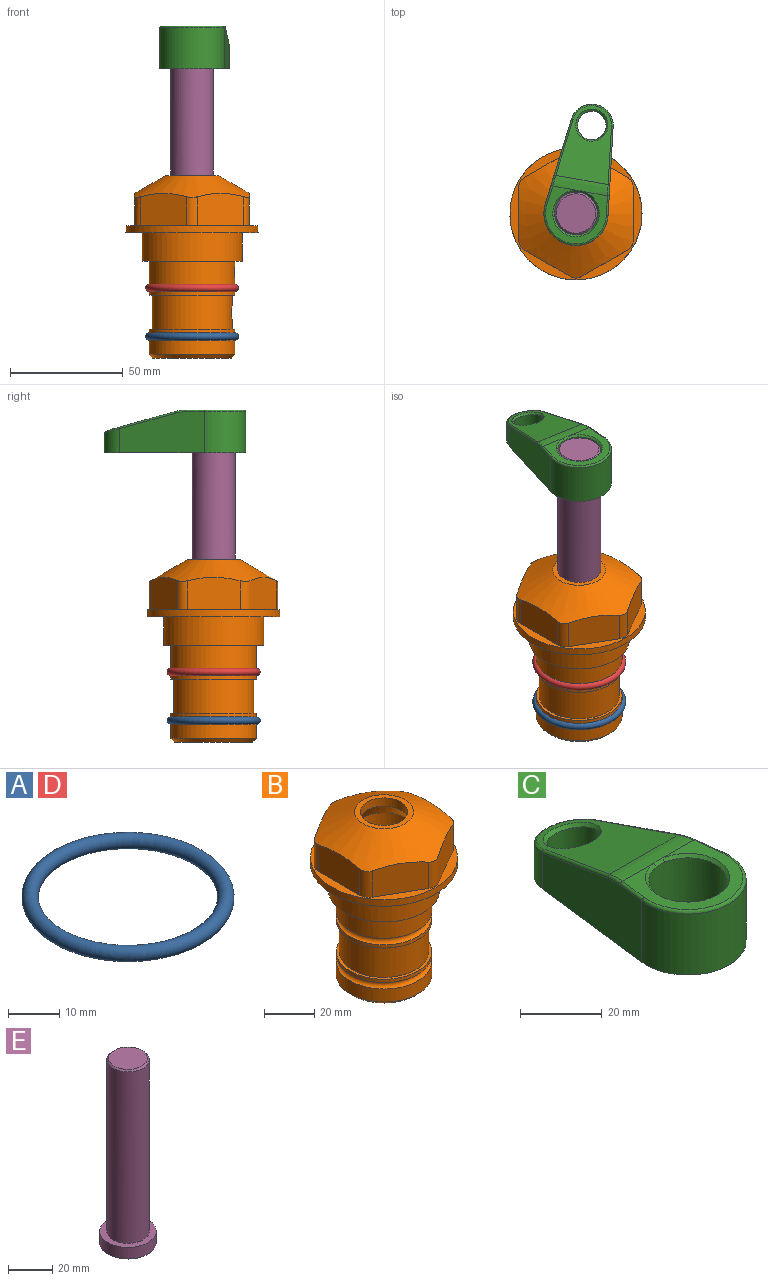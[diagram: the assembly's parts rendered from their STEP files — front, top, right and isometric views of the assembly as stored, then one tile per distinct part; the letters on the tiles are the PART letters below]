
ASSEMBLY  parts=5 mates=4
PART A: 1 faces, bbox 44.7x44.7x3.2 mm
  f0: torus R=19.05mm, axis (0,0,1), area 1193.9mm2
PART B: 36 faces, bbox 58.7x58.7x81 mm
  f0: cylinder r=17.78mm len=35.56mm, axis (0,0,1), area 1670.8mm2, adj f23,f24,f31
  f1: cylinder r=19.05mm len=38.1mm, axis (0,0,1), area 1191.9mm2, adj f26,f27,f30
  f2: plane 58.66x58.66mm, normal (0,0,-1), area 1150.6mm2, adj f3,f28
  f3: cylinder r=29.33mm len=58.66mm, axis (0,0,-1), area 585.1mm2, adj f2,f4
  f4: plane 58.66x58.66mm, normal (0,0,1), area 475.9mm2, adj f3,f5,f6,f7,f8,f9,f10,f11
  f5: plane 20.32x14.34mm, normal (-0.5,0.87,0), area 324.4mm2, adj f4,f15,f16,f17
  f6: plane 20.32x14.34mm, normal (0.5,0.87,0), area 324.4mm2, adj f4,f14,f15,f17
  f7: plane 23.48x14.34mm, normal (1,0,0), area 324.4mm2, adj f4,f13,f14,f17
  f8: plane 20.32x14.34mm, normal (0.5,-0.87,0), area 324.4mm2, adj f4,f12,f13,f17
  f9: plane 20.32x14.34mm, normal (-0.5,-0.87,0), area 324.4mm2, adj f4,f11,f12,f17
  f10: plane 23.48x14.34mm, normal (-1,0,0), area 324.4mm2, adj f4,f11,f16,f17
  f11: cylinder r=5.08mm len=12.85mm, axis (0,0,-1), area 67.2mm2, adj f4,f9,f10,f17
  f12: cylinder r=5.08mm len=12.85mm, axis (0,0,-1), area 67.2mm2, adj f4,f8,f9,f17
  f13: cylinder r=5.08mm len=12.85mm, axis (0,0,-1), area 67.2mm2, adj f4,f7,f8,f17
  f14: cylinder r=5.08mm len=12.85mm, axis (0,0,-1), area 67.2mm2, adj f4,f6,f7,f17
  f15: cylinder r=5.08mm len=12.85mm, axis (0,0,-1), area 67.2mm2, adj f4,f5,f6,f17
  f16: cylinder r=5.08mm len=12.85mm, axis (0,0,-1), area 67.2mm2, adj f4,f5,f10,f17
  f17: cone r=11.73mm half-angle=60deg, axis (0,0,-1), area 2071.8mm2, adj f5,f6,f7,f8,f9,f10,f11,f12
  f18: plane 23.46x23.46mm, normal (0,0,1), area 147.4mm2, adj f17,f35
  f19: plane 34.93x34.93mm, normal (0,0,-1), area 958mm2, adj f29
  f20: cylinder r=19.05mm len=38.1mm, axis (0,0,1), area 760.1mm2, adj f21,f29
  f21: torus R=19.05mm, axis (0,0,1), area 565.3mm2, adj f20,f22
  f22: cylinder r=19.05mm len=38.1mm, axis (0,0,1), area 190mm2, adj f21,f23
  f23: plane 38.1x38.1mm, normal (0,0,1), area 146.9mm2, adj f0,f22
  f24: plane 38.1x38.1mm, normal (0,0,-1), area 146.9mm2, adj f0,f25
  f25: cylinder r=19.05mm len=38.1mm, axis (0,0,1), area 190mm2, adj f24,f26
  f26: torus R=19.05mm, axis (0,0,1), area 565.3mm2, adj f1,f25
  f27: plane 44.45x44.45mm, normal (0,0,-1), area 411.7mm2, adj f1,f28
  f28: cylinder r=22.23mm len=44.45mm, axis (0,0,1), area 1773.5mm2, adj f2,f27
  f29: cone r=19.05mm half-angle=45deg, axis (0,0,1), area 257.5mm2, adj f19,f20
  f30: cylinder r=3.17mm len=6.75mm, axis (-1,0,0), area 128mm2, adj f1,f33
  f31: cylinder r=3.17mm len=6.35mm, axis (-1,0,0), area 102.5mm2, adj f0,f33
  f32: plane 25.4x25.4mm, normal (0,0,1), area 506.7mm2, adj f33
  f33: cylinder r=12.7mm len=66.42mm, axis (0,0,-1), area 5236.2mm2, adj f30,f31,f32,f34
  f34: cone r=9.53mm half-angle=30deg, axis (0,0,-1), area 443.4mm2, adj f33,f35
  f35: cylinder r=9.53mm len=19.05mm, axis (0,0,-1), area 240.9mm2, adj f18,f34
PART C: 31 faces, bbox 31.7x65.5x19.8 mm
  f0: plane 39.12x18.26mm, normal (0.99,0.12,0), area 612.2mm2, adj f1,f4,f7,f11,f13,f15
  f1: cylinder r=9.53mm len=18.91mm, axis (0,0,-1), area 296.1mm2, adj f0,f2,f7,f17
  f2: plane 39.12x18.26mm, normal (-0.99,0.12,0), area 612.2mm2, adj f1,f4,f7,f12,f14,f16
  f3: cylinder r=6.35mm len=12.7mm, axis (0,0,-1), area 362.4mm2, adj f7,f18
  f4: cylinder r=14.29mm len=28.58mm, axis (0,0,-1), area 882.2mm2, adj f0,f2,f7,f10
  f5: cylinder r=9.53mm len=19.05mm, axis (0,0,-1), area 1092.6mm2, adj f7,f19,f20
  f6: plane 26.99x23.69mm, normal (0,0,1), area 216.2mm2, adj f9,f10,f11,f12,f19
  f7: plane 63.5x28.58mm, normal (0,0,-1), area 661.8mm2, adj f0,f1,f2,f3,f4,f5,f22,f23
  f8: plane 33.52x23.6mm, normal (0,0.26,0.97), area 486mm2, adj f9,f15,f16,f17,f18
  f9: cylinder r=19.05mm len=24.72mm, axis (1,0,0), area 120.4mm2, adj f6,f8,f13,f14,f20
  f10: torus R=13.49mm, axis (0,0,1), area 59mm2, adj f4,f6,f11,f12
  f11: cylinder r=0.79mm len=8.67mm, axis (0.12,-0.99,0), area 10.8mm2, adj f0,f6,f10,f13
  f12: cylinder r=0.79mm len=8.67mm, axis (0.12,0.99,0), area 10.8mm2, adj f2,f6,f10,f14
  f13: bspline ~4.95x1.42mm, area 6.1mm2, adj f0,f9,f11,f15
  f14: bspline ~4.95x1.42mm, area 6.1mm2, adj f2,f9,f12,f16
  f15: cylinder r=0.79mm len=25.95mm, axis (0.12,-0.96,0.26), area 32.9mm2, adj f0,f8,f13,f17
  f16: cylinder r=0.79mm len=25.95mm, axis (0.12,0.96,-0.26), area 32.9mm2, adj f2,f8,f14,f17
  f17: bspline ~18.91x8.38mm, area 30mm2, adj f1,f8,f15,f16
  f18: bspline ~14.29x14.29mm, area 48.3mm2, adj f3,f8
  f19: cone r=9.53mm half-angle=45deg, axis (0,0,1), area 66.5mm2, adj f5,f6,f20
  f20: bspline ~3.22x0.96mm, area 3.5mm2, adj f5,f9,f19
  f21: plane 2.75x2.72mm, normal (0,0,-1), area 2.9mm2, adj f23,f25,f28
  f22: plane 23.05x15.88mm, normal (-0.99,-0.12,0), area 323.6mm2, adj f7,f25,f26,f27,f28,f29
  f23: plane 23.05x15.88mm, normal (0.99,-0.12,0), area 323.6mm2, adj f7,f21,f25,f27,f28,f30
  f24: cylinder r=9.53mm len=10.69mm, axis (0,0,-1), area 114.7mm2, adj f7,f27,f29,f30
  f25: cylinder r=12.7mm len=20.59mm, axis (0,0,-1), area 381.1mm2, adj f7,f21,f22,f23,f26,f28
  f26: plane 2.75x2.72mm, normal (0,0,-1), area 2.9mm2, adj f22,f25,f28
  f27: plane 19.72x18.37mm, normal (0,-0.26,-0.97), area 291.8mm2, adj f22,f23,f24,f28,f29,f30
  f28: cylinder r=15.88mm len=19.92mm, axis (1,0,0), area 54.8mm2, adj f21,f22,f23,f25,f26,f27
  f29: cylinder r=1.59mm len=11mm, axis (0,0,-1), area 34.7mm2, adj f7,f22,f24,f27
  f30: cylinder r=1.59mm len=11mm, axis (0,0,-1), area 34.7mm2, adj f7,f23,f24,f27
PART D: same geometry as A
PART E: 6 faces, bbox 25.4x25.4x101.6 mm
  f0: plane 17.46x17.46mm, normal (0,0,1), area 239.5mm2, adj f5
  f1: plane 25.4x25.4mm, normal (0,0,-1), area 506.7mm2, adj f2
  f2: cylinder r=12.7mm len=25.4mm, axis (0,0,1), area 506.7mm2, adj f1,f3
  f3: plane 25.4x25.4mm, normal (0,0,1), area 221.7mm2, adj f2,f4
  f4: cylinder r=9.53mm len=94.46mm, axis (0,0,1), area 5653mm2, adj f3,f5
  f5: cone r=8.73mm half-angle=45deg, axis (0,0,-1), area 64.4mm2, adj f0,f4
PLACE A t=(0,0,-21.59)mm
PLACE B at identity fixed
PLACE C rot(axis=(0,0,-1),10.2deg) t=(0,0,28.35)mm
PLACE D at identity
PLACE E rot(axis=(0,0,-1),10.2deg) t=(0,0,27.55)mm
MATE cylindrical E.f2 <-> B.f0  axis (0,0,-1) through (0,0,-10.55)mm
MATE fastened D.f0 <-> B.f0  axis (0,0,1) through (0,0,-24.51)mm
MATE fastened C.f4 <-> E.f2  axis (0,0,1) through (0,0,91.05)mm
MATE fastened A.f0 <-> B.f0  axis (0,0,1) through (0,0,-46.1)mm
